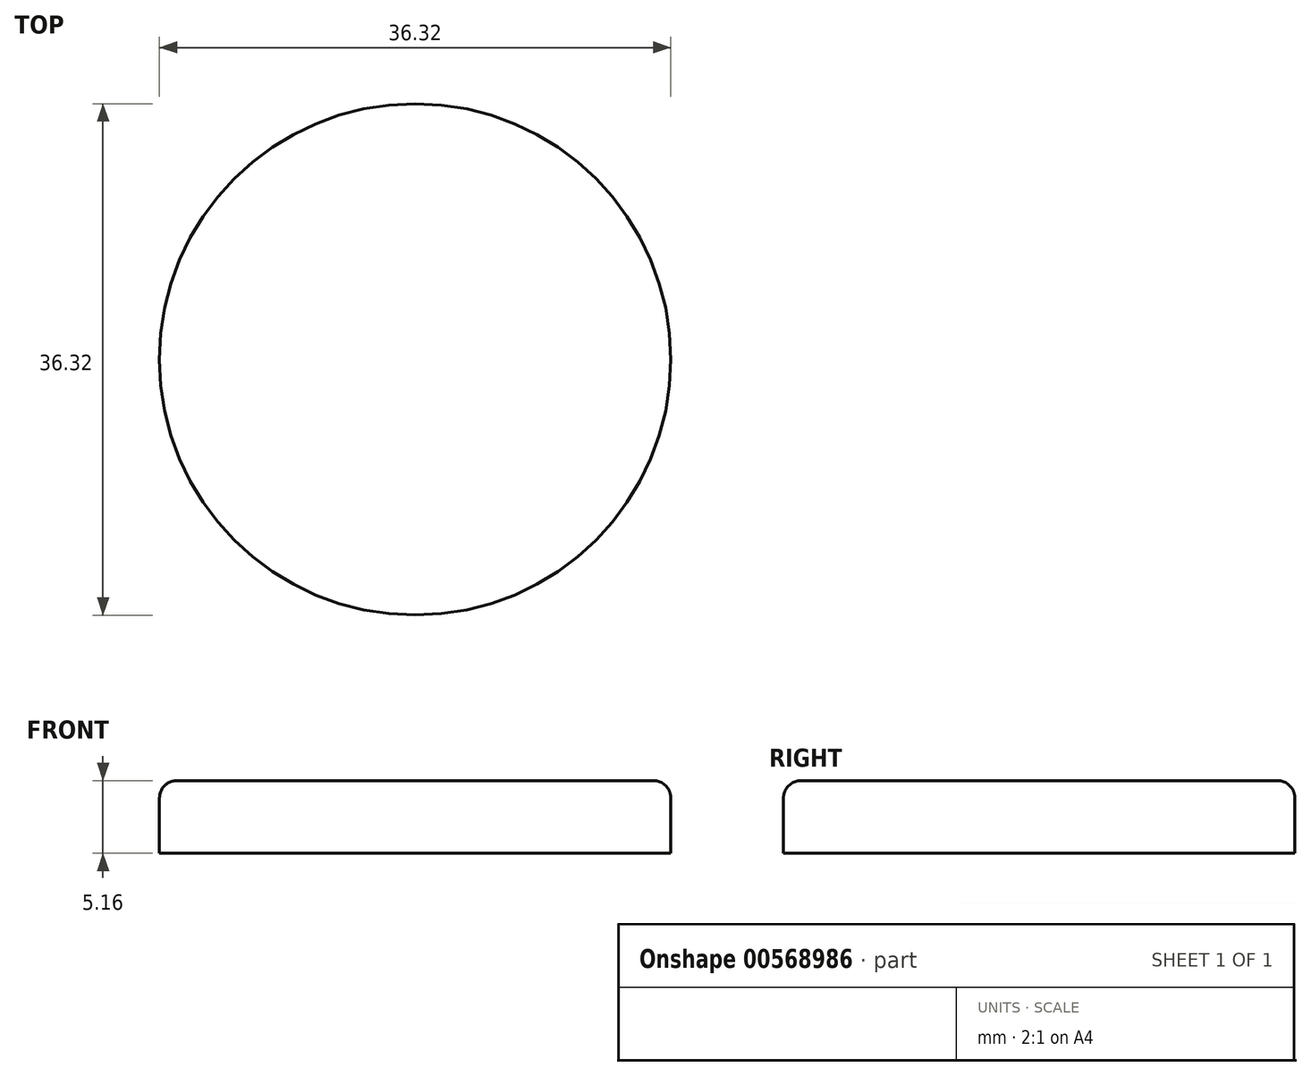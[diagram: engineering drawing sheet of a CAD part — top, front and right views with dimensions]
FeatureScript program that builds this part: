
annotation { "Feature Type Name" : "Feature", "Feature Type Description" : "" }
export const myFeature = defineFeature(function(context is Context, id is Id, definition is map)
    precondition{}
    {
        {
            var Q0;
            Q0=qCreatedBy(makeId("Front.planeOp"),FACE);
            var sketch = newSketch(context, id + "F0", { "sketchPlane" : qUnion([Q0])});
            skLineSegment(sketch, "E0.bottom", {"start": v(-18.16, 3.68) * mm, "end": v(18.16, 3.68) * mm});
            skLineSegment(sketch, "E0.top", {"start": v(-18.16, -1.48) * mm, "end": v(18.16, -1.48) * mm});
            skLineSegment(sketch, "E0.left", {"start": v(-18.16, 3.68) * mm, "end": v(-18.16, -1.48) * mm});
            skLineSegment(sketch, "E0.right", {"start": v(18.16, 3.68) * mm, "end": v(18.16, -1.48) * mm});
            skLineSegment(sketch, "E1", {"start": v(0, 3.68) * mm, "end": v(0, -1.48) * mm});
            skSolve(sketch);
        }
        {
            var Q0;
            {var subQ0=sQuery(id+"F0.wireOp",EDGE,"E0.left");Q0=makeQuery(id+"F0.imprint","IMPRINT",FACE,{"disambiguationData":[TD([[makeQuery(id+"F0.imprint","IMPRINT",EDGE,{"derivedFrom":subQ0}),1.0]])]});}
            var Q1;
            Q1=sQuery(id+"F0.wireOp",EDGE,"E1");
            revolve(context, id + "F1", {"entities" : qUnion([Q0]), "axis" : qUnion([Q1]), "revolveType" : RevolveType.FULL});
        }
        {
            var Q0;
            Q0=makeQuery(id+"F1.opRevolve","SWEPT_EDGE",EDGE,{"disambiguationData":[OSD([sQuery(id+"F0.wireOp",EDGE,"E0.bottom"),sQuery(id+"F0.wireOp",EDGE,"E0.left")])]});
            fillet(context, id + "F2", {"entities" : qUnion([Q0]), "radius" : 1.23 * mm, "tangentPropagation" : true, "allowEdgeOverflow" : false});
        }
    });
